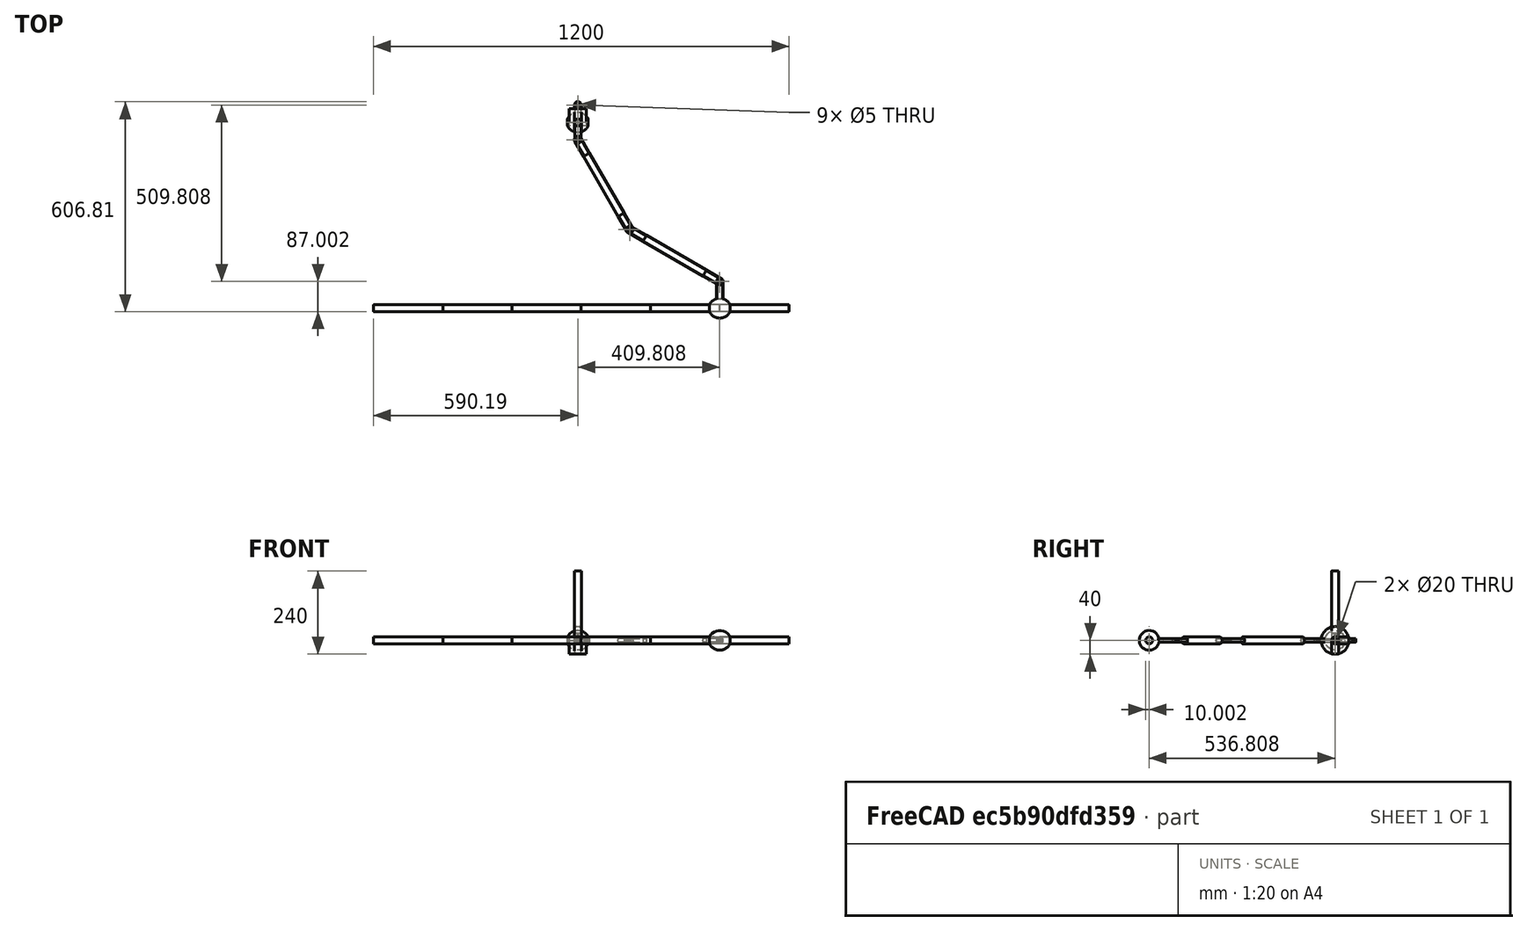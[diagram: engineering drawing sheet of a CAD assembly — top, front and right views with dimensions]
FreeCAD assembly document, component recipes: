
FREECAD ASSEMBLY — COMPONENT RECIPES ("Demo8Trans")

This assembly document has 7 components, labeled P0..P6 below (a component is one placed body or linked part). 7 of them carry a construction recipe — the FreeCAD feature program that regenerates the part from scratch, quoted from this document or its linked companion documents; the rest are supplied as boundary geometry only. No exploded tour is included for this assembly.
COMPONENT P0 — recipe-attached ("Weight", modeled in this document).
Construction recipe (the document's own serialized feature program — sketch geometry with constraints, then the solid features built on it; lengths are millimeters unless a unit is written):

FEATURE [Sketcher::SketchObject] Sketch
  FullyConstrained = true
  MapMode = 5
  Support = -> [XY_Plane]
  sketch-geometry (2):
    g0: LineSegment StartX=-30 StartY=10 StartZ=0 EndX=30 EndY=10 EndZ=0
    g1: ArcOfCircle CenterX=0 CenterY=-5 CenterZ=0 NormalX=0 NormalY=0 NormalZ=1 AngleXU=0 Radius=33.541 StartAngle=0.463648 EndAngle=2.67795
  constraints (7):
    c: Horizontal(g0)
    c: DistanceY(g-1,g0) = 10
    c: DistanceX(g-1,g0) = 30
    c: PointOnObject(g1,g-2)
    c: DistanceY(g1,g-1) = 5
    c: Coincident(g1,g0)
    c: Coincident(g1,g0)
FEATURE [PartDesign::Revolution] Revolution
  Angle = 360
  Axis = (1,0,0)
  Base = (0,0,0)
  Profile = -> Sketch
  ReferenceAxis = -> Sketch [H_Axis]
FEATURE [PartDesign::CoordinateSystem] WeightTop
  AttacherType = Attacher::AttachEngine3D
  MapMode = 11
  Placement = pos=(30,-1.8e-15,0) rot=(0.707107,0,0.707107;3.14159rad)
  Support = -> [Revolution]
FEATURE [PartDesign::CoordinateSystem] WeightBot
  AttacherType = Attacher::AttachEngine3D
  MapMode = 11
  Placement = pos=(-30,0,0) rot=(0.707107,0,0.707107;3.14159rad)
  Support = -> [Revolution]
FEATURE [PartDesign::CoordinateSystem] WeightLCS
  AttacherType = Attacher::AttachEngine3D
  MapMode = 2
  Support = -> [Body003]
FEATURE [PartDesign::Body] Body  label="Weight"
  Group = -> [Sketch,Revolution,WeightLCS,WeightTop,WeightBot]
  Origin = -> Origin
  Tip = -> Revolution
COMPONENT P1 — recipe-attached ("Rod", modeled in this document).
Construction recipe (the document's own serialized feature program — sketch geometry with constraints, then the solid features built on it; lengths are millimeters unless a unit is written):

FEATURE [Sketcher::SketchObject] Sketch001
  FullyConstrained = true
  MapMode = 5
  Support = -> [XY_Plane001]
  sketch-geometry (1):
    g0: Circle CenterX=0 CenterY=0 CenterZ=0 NormalX=0 NormalY=0 NormalZ=1 AngleXU=0 Radius=10
  constraints (2):
    c: Coincident(g0,g-1)
    c: Diameter(g0) = 20
FEATURE [PartDesign::Pad] Pad
  Direction = (0,0,1)
  Length = 200
  Length2 = 10
  Profile = -> Sketch001
  ReferenceAxis = -> Sketch001 [N_Axis]
  Type = 0
FEATURE [PartDesign::CoordinateSystem] RodTop
  AttacherType = Attacher::AttachEngine3D
  MapMode = 11
  Placement = pos=(0,0,200) rot=(0,0,1;1.5708rad)
  Support = -> [Pad]
FEATURE [PartDesign::CoordinateSystem] RodBottom
  AttacherType = Attacher::AttachEngine3D
  MapMode = 11
  Placement = pos=(0,0,0) rot=(0,0,1;1.5708rad)
  Support = -> [Pad]
FEATURE [PartDesign::Body] Body001  label="Rod"
  Group = -> [Sketch001,Pad,RodTop,RodBottom]
  Origin = -> Origin001
  Tip = -> Pad
COMPONENT P2 — recipe-attached ("LugBody", modeled in this document).
Construction recipe (the document's own serialized feature program — sketch geometry with constraints, then the solid features built on it; lengths are millimeters unless a unit is written):

FEATURE [Sketcher::SketchObject] Sketch002
  FullyConstrained = true
  MapMode = 5
  Support = -> [XY_Plane002]
  sketch-geometry (5):
    g0: LineSegment StartX=-10 StartY=0 StartZ=0 EndX=-10 EndY=50 EndZ=0
    g1: ArcOfCircle CenterX=0 CenterY=50 CenterZ=0 NormalX=0 NormalY=0 NormalZ=1 AngleXU=0 Radius=10 StartAngle=1e-16 EndAngle=3.14159
    g2: LineSegment StartX=10 StartY=50 StartZ=0 EndX=10 EndY=0 EndZ=0
    g3: LineSegment StartX=10 StartY=0 StartZ=0 EndX=-10 EndY=0 EndZ=0
    g4: Circle CenterX=0 CenterY=50 CenterZ=0 NormalX=0 NormalY=0 NormalZ=1 AngleXU=0 Radius=2.5
  constraints (13):
    c: PointOnObject(g0,g-1)
    c: Vertical(g0)
    c: Tangent(g0,g1) = 1.5708
    c: Tangent(g1,g2) = 1.5708
    c: Coincident(g2,g3)
    c: Coincident(g3,g0)
    c: Horizontal(g3)
    c: PointOnObject(g1,g-2)
    c: Vertical(g2)
    c: Diameter(g1) = 20
    c: Distance(g2) = 50
    c: Coincident(g4,g1)
    c: Diameter(g4) = 5
FEATURE [PartDesign::Pad] Pad001
  Direction = (0,0,1)
  Length = 10
  Length2 = 10
  Midplane = true
  Profile = -> Sketch002
  ReferenceAxis = -> Sketch002 [N_Axis]
  Type = 0
FEATURE [PartDesign::Body] Body002  label="LugBody"
  Group = -> [Sketch002,Pad001]
  Origin = -> Origin002
  Tip = -> Pad001
COMPONENT P3 — recipe-attached ("LugCylinder", modeled in this document).
Construction recipe (the document's own serialized feature program — sketch geometry with constraints, then the solid features built on it; lengths are millimeters unless a unit is written):

FEATURE [Sketcher::SketchObject] Sketch003
  FullyConstrained = true
  MapMode = 5
  Placement = pos=(0,0,0) rot=(1,0,0;1.5708rad)
  Support = -> [XZ_Plane003]
  sketch-geometry (1):
    g0: Circle CenterX=0 CenterY=0 CenterZ=0 NormalX=0 NormalY=0 NormalZ=1 AngleXU=0 Radius=10
  constraints (2):
    c: Coincident(g0,g-1)
    c: Diameter(g0) = 20
FEATURE [PartDesign::Pad] Pad002
  Direction = (0,-1,-2e-16)
  Length = 60
  Length2 = 10
  Placement = pos=(0,0,0) rot=(1,0,0;1.5708rad)
  Profile = -> Sketch003
  ReferenceAxis = -> Sketch003 [N_Axis]
  Reversed = true
  Type = 0
FEATURE [PartDesign::Boolean] Boolean
  BaseFeature = -> Pad002
  Group = -> [Body002]
  Type = 2
FEATURE [PartDesign::CoordinateSystem] LugHole
  AttacherType = Attacher::AttachEngine3D
  MapMode = 11
  Placement = pos=(0,50,5) rot=(0,0,1;1.5708rad)
  Support = -> [Boolean]
FEATURE [PartDesign::CoordinateSystem] LugFace
  AttacherType = Attacher::AttachEngine3D
  MapMode = 5
  Placement = pos=(0,0,0) rot=(1,0,0;1.5708rad)
  Support = -> [Boolean]
FEATURE [PartDesign::CoordinateSystem] LugRot30
  AttacherType = Attacher::AttachEngine3D
  AttachmentOffset = pos=(0,0,0) rot=(0,0,1;0.523599rad)
  MapMode = 11
  Placement = pos=(0,50,5) rot=(0,0,1;2.0944rad)
  Support = -> [Boolean]
FEATURE [PartDesign::CoordinateSystem] LugRot60
  AttacherType = Attacher::AttachEngine3D
  AttachmentOffset = pos=(0,0,0) rot=(0,0,1;1.0472rad)
  MapMode = 11
  Placement = pos=(0,50,5) rot=(0,0,1;2.61799rad)
  Support = -> [Boolean]
FEATURE [PartDesign::Body] Body003  label="LugCylinder"
  Group = -> [Sketch003,Pad002,Boolean,LugHole,LugFace,LugRot30,LugRot60]
  Origin = -> Origin003
  Tip = -> Boolean
COMPONENT P4 — recipe-attached ("BobBody", modeled in this document).
Construction recipe (the document's own serialized feature program — sketch geometry with constraints, then the solid features built on it; lengths are millimeters unless a unit is written):

FEATURE [Sketcher::SketchObject] Sketch004
  FullyConstrained = true
  MapMode = 5
  Support = -> [XY_Plane004]
  sketch-geometry (4):
    g0: LineSegment StartX=-10 StartY=0 StartZ=0 EndX=-10 EndY=30 EndZ=0
    g1: ArcOfCircle CenterX=0 CenterY=30 CenterZ=0 NormalX=0 NormalY=0 NormalZ=1 AngleXU=0 Radius=10 StartAngle=2e-16 EndAngle=3.14159
    g2: LineSegment StartX=10 StartY=30 StartZ=0 EndX=10 EndY=0 EndZ=0
    g3: LineSegment StartX=10 StartY=0 StartZ=0 EndX=-10 EndY=0 EndZ=0
  constraints (11):
    c: PointOnObject(g0,g-1)
    c: Vertical(g0)
    c: Tangent(g0,g1) = 1.5708
    c: Tangent(g1,g2) = 1.5708
    c: Coincident(g2,g3)
    c: Coincident(g3,g0)
    c: Vertical(g2)
    c: PointOnObject(g1,g-2)
    c: Diameter(g1) = 20
    c: Distance(g0) = 30
    c: PointOnObject(g2,g-1)
FEATURE [PartDesign::Revolution] Revolution001
  Angle = 360
  Axis = (1,0,0)
  Base = (0,0,0)
  Profile = -> Sketch004
  ReferenceAxis = -> Sketch004 [H_Axis]
FEATURE [PartDesign::CoordinateSystem] BobBody  label="BobBody001"
  AttacherType = Attacher::AttachEngine3D
  MapMode = 11
  Placement = pos=(-10,0,0) rot=(0.707107,0,0.707107;3.14159rad)
  Support = -> [Revolution001]
FEATURE [PartDesign::Body] Body004  label="BobBody"
  Group = -> [Sketch004,Revolution001,BobBody]
  Origin = -> Origin004
  Tip = -> Revolution001
COMPONENT P5 — recipe-attached ("GroundBody", modeled in this document).
Construction recipe (the document's own serialized feature program — sketch geometry with constraints, then the solid features built on it; lengths are millimeters unless a unit is written):

FEATURE [Sketcher::SketchObject] Sketch005
  FullyConstrained = true
  MapMode = 5
  Support = -> [XY_Plane005]
  sketch-geometry (4):
    g0: LineSegment StartX=-25 StartY=10 StartZ=0 EndX=25 EndY=10 EndZ=0
    g1: LineSegment StartX=25 StartY=10 StartZ=0 EndX=25 EndY=-10 EndZ=0
    g2: LineSegment StartX=25 StartY=-10 StartZ=0 EndX=-25 EndY=-10 EndZ=0
    g3: LineSegment StartX=-25 StartY=-10 StartZ=0 EndX=-25 EndY=10 EndZ=0
  constraints (11):
    c: Coincident(g0,g1)
    c: Coincident(g1,g2)
    c: Coincident(g2,g3)
    c: Coincident(g3,g0)
    c: Horizontal(g0)
    c: Horizontal(g2)
    c: Vertical(g1)
    c: Vertical(g3)
    c: DistanceY(g2,g0) = 20
    c: DistanceX(g0,g0) = 50
    c: Symmetric(g0,g1,g-1)
FEATURE [PartDesign::Pad] Pad003
  Direction = (0,0,1)
  Length = 40
  Length2 = 10
  Profile = -> Sketch005
  ReferenceAxis = -> Sketch005 [N_Axis]
  Reversed = true
  Type = 0
FEATURE [PartDesign::CoordinateSystem] GroundLCS
  AttacherType = Attacher::AttachEngine3D
  MapMode = 5
  Placement = pos=(0,0,-40) rot=(1,0,0;3.14159rad)
  Support = -> [Pad003]
FEATURE [PartDesign::Body] Body005  label="GroundBody"
  Group = -> [Sketch005,Pad003,GroundLCS]
  Origin = -> Origin005
  Tip = -> Pad003
COMPONENT P6 — recipe-attached ("Spacer", modeled in this document).
Construction recipe (the document's own serialized feature program — sketch geometry with constraints, then the solid features built on it; lengths are millimeters unless a unit is written):

FEATURE [Sketcher::SketchObject] Sketch006
  FullyConstrained = true
  MapMode = 5
  Support = -> [XY_Plane007]
  sketch-geometry (2):
    g0: Circle CenterX=0 CenterY=0 CenterZ=0 NormalX=0 NormalY=0 NormalZ=1 AngleXU=0 Radius=10
    g1: Circle CenterX=0 CenterY=0 CenterZ=0 NormalX=0 NormalY=0 NormalZ=1 AngleXU=0 Radius=2.5
  constraints (4):
    c: Coincident(g0,g-1)
    c: Coincident(g1,g0)
    c: Diameter(g0) = 20
    c: Diameter(g1) = 5
FEATURE [PartDesign::Pad] Pad004
  Direction = (0,0,1)
  Length = 20
  Length2 = 10
  Profile = -> Sketch006
  ReferenceAxis = -> Sketch006 [N_Axis]
  Type = 0
FEATURE [PartDesign::CoordinateSystem] SpacerTop
  AttacherType = Attacher::AttachEngine3D
  MapMode = 11
  Placement = pos=(0,0,20) rot=(0,0,1;1.5708rad)
  Support = -> [Pad004]
FEATURE [PartDesign::Body] Body006  label="Spacer"
  Group = -> [Sketch006,Pad004,SpacerTop]
  Origin = -> Origin007
  Tip = -> Pad004
PROVENANCE & LICENSES
A FreeCAD (.FCStd) document from a public repository crawl; recipes are the document's own serialized feature recipes (and, for linked parts, companion documents' recipes).
License: gpl-3.0.
